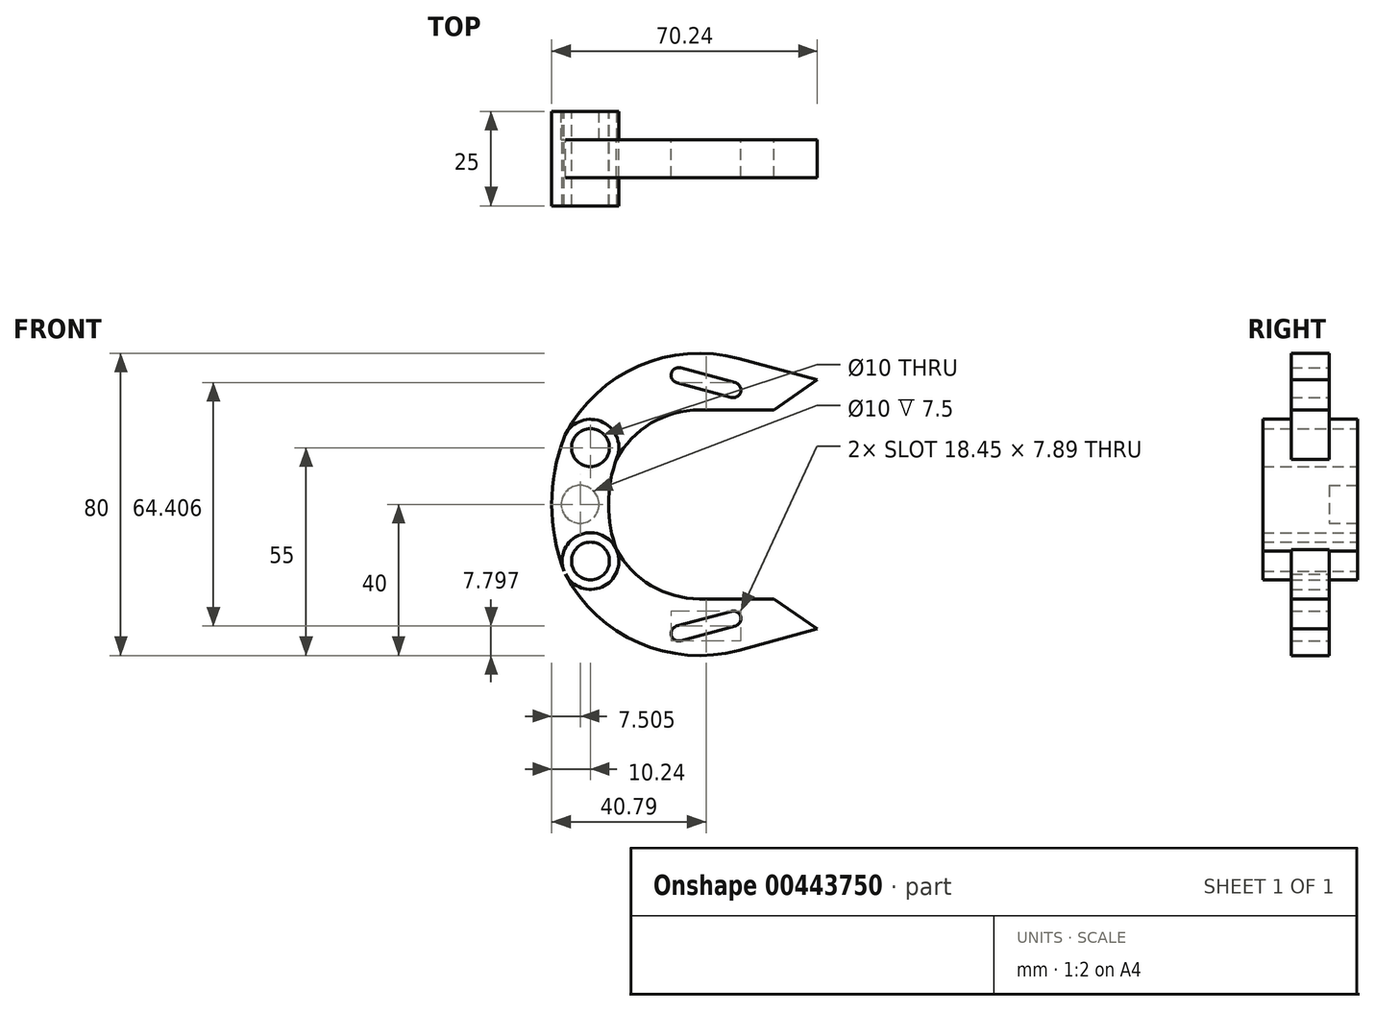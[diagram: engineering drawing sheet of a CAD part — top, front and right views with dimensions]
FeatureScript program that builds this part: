
annotation { "Feature Type Name" : "Feature", "Feature Type Description" : "" }
export const myFeature = defineFeature(function(context is Context, id is Id, definition is map)
    precondition{}
    {
        {
            var Q0;
            Q0=qCreatedBy(makeId("Front.planeOp"),FACE);
            var sketch = newSketch(context, id + "F0", { "sketchPlane" : qUnion([Q0])});
            skLineSegment(sketch, "E0", {"start": v(0, 15) * mm, "end": v(0, -15) * mm, "construction": true});
            skCircle(sketch, "E1", {"center": v(0, 15) * mm, "radius": 7.5 * mm});
            skCircle(sketch, "E2", {"center": v(0, -15) * mm, "radius": 7.5 * mm});
            skArc(sketch, "E3", {"start": v(-7.02, 17.65) * mm, "mid": v(-10.24, 0) * mm, "end": v(-7.02, -17.65) * mm});
            skArc(sketch, "E4", {"start": v(7.02, 12.35) * mm, "mid": v(4.76, 0) * mm, "end": v(7.02, -12.35) * mm});
            skCircle(sketch, "E5", {"center": v(0, 15) * mm, "radius": 5 * mm});
            skCircle(sketch, "E6", {"center": v(0, -15) * mm, "radius": 5 * mm});
            skArc(sketch, "E7", {"start": v(39.29, 38.6) * mm, "mid": v(12.77, 36.63) * mm, "end": v(-6.65, 18.46) * mm});
            skArc(sketch, "E8", {"start": v(28.83, 25) * mm, "mid": v(15.86, 21.37) * mm, "end": v(6.65, 11.54) * mm});
            skLineSegment(sketch, "E9", {"start": v(28.83, 25) * mm, "end": v(48.5, 25) * mm});
            skLineSegment(sketch, "E10", {"start": v(48.5, 25) * mm, "end": v(60, 33) * mm});
            skLineSegment(sketch, "E11", {"start": v(60, 33) * mm, "end": v(39.29, 38.6) * mm});
            skLineSegment(sketch, "E12", {"start": v(39.29, 38.6) * mm, "end": v(37.79, 30.24) * mm, "construction": true});
            skLineSegment(sketch, "E13", {"start": v(37.79, 30.24) * mm, "end": v(23.31, 34.16) * mm, "construction": true});
            skArc(sketch, "E14", {"start": v(23.83, 36.1) * mm, "mid": v(21.38, 34.69) * mm, "end": v(22.79, 32.23) * mm});
            skArc(sketch, "E15", {"start": v(37.27, 28.31) * mm, "mid": v(39.74, 29.8) * mm, "end": v(38.14, 32.21) * mm});
            skLineSegment(sketch, "E16.0", {"start": v(37.27, 28.31) * mm, "end": v(22.79, 32.23) * mm});
            skLineSegment(sketch, "E17.0", {"start": v(38.31, 32.17) * mm, "end": v(23.83, 36.1) * mm});
            skLineSegment(sketch, "E18.MirrorCS", {"start": v(38.31, -32.17) * mm, "end": v(23.83, -36.1) * mm});
            skLineSegment(sketch, "E19.MirrorCS", {"start": v(37.79, -30.24) * mm, "end": v(23.31, -34.16) * mm, "construction": true});
            skArc(sketch, "E20.MirrorCS", {"start": v(23.83, -36.1) * mm, "mid": v(21.38, -34.69) * mm, "end": v(22.79, -32.23) * mm});
            skLineSegment(sketch, "E21.MirrorCS", {"start": v(60, -33) * mm, "end": v(39.29, -38.6) * mm});
            skArc(sketch, "E22.MirrorCS", {"start": v(39.29, -38.6) * mm, "mid": v(12.77, -36.63) * mm, "end": v(-6.65, -18.46) * mm});
            skLineSegment(sketch, "E23.MirrorCS", {"start": v(48.5, -25) * mm, "end": v(60, -33) * mm});
            skArc(sketch, "E24.MirrorCS", {"start": v(37.27, -28.31) * mm, "mid": v(39.74, -29.8) * mm, "end": v(38.14, -32.21) * mm});
            skArc(sketch, "E25.MirrorCS", {"start": v(28.83, -25) * mm, "mid": v(15.86, -21.37) * mm, "end": v(6.65, -11.54) * mm});
            skLineSegment(sketch, "E26.MirrorCS", {"start": v(28.83, -25) * mm, "end": v(48.5, -25) * mm});
            skLineSegment(sketch, "E27.MirrorCS", {"start": v(37.27, -28.31) * mm, "end": v(22.79, -32.23) * mm});
            skLineSegment(sketch, "E28.MirrorCS", {"start": v(39.29, -38.6) * mm, "end": v(37.79, -30.24) * mm, "construction": true});
            skSolve(sketch);
        }
        {
            var Q0;
            {var subQ0=sQuery(id+"F0.wireOp",EDGE,"E4");var subQ1=sQuery(id+"F0.wireOp",EDGE,"E1");var subQ2=makeQuery(id+"F0.imprint","INTERSECT",VERTEX,{"derivedFrom":[subQ1,subQ0]});Q0=makeQuery(id+"F0.imprint","IMPRINT",FACE,{"disambiguationData":[TD([[makeQuery(id+"F0.imprint","IMPRINT",EDGE,{"disambiguationData":[TD([[subQ2,1.0]])],"derivedFrom":subQ1}),-1.0]])]});}
            var Q1;
            {var subQ0=sQuery(id+"F0.wireOp",EDGE,"E2");var subQ1=sQuery(id+"F0.wireOp",EDGE,"E4");var subQ2=makeQuery(id+"F0.imprint","INTERSECT",VERTEX,{"derivedFrom":[subQ1,subQ0]});Q1=makeQuery(id+"F0.imprint","IMPRINT",FACE,{"disambiguationData":[TD([[makeQuery(id+"F0.imprint","IMPRINT",EDGE,{"disambiguationData":[TD([[subQ2,1.0]])],"derivedFrom":subQ1}),-1.0]])]});}
            var Q2;
            Q2=makeQuery(id+"F0.imprint","IMPRINT",FACE,{"disambiguationData":[TD([[makeQuery(id+"F0.imprint","IMPRINT",EDGE,{"derivedFrom":sQuery(id+"F0.wireOp",EDGE,"E6")}),1.0]])]});
            var Q3;
            {var subQ0=sQuery(id+"F0.wireOp",EDGE,"E3");Q3=makeQuery(id+"F0.imprint","IMPRINT",FACE,{"disambiguationData":[TD([[makeQuery(id+"F0.imprint","IMPRINT",EDGE,{"derivedFrom":subQ0}),1.0]])]});}
            var Q4;
            Q4=makeQuery(id+"F0.imprint","IMPRINT",FACE,{"disambiguationData":[TD([[makeQuery(id+"F0.imprint","IMPRINT",EDGE,{"derivedFrom":sQuery(id+"F0.wireOp",EDGE,"E5")}),-1.0]])]});
            extrude(context, id + "F1", {"entities" : qUnion([Q0, Q1, Q2, Q3, Q4]), "endBound" : BoundingType.SYMMETRIC, "depth" : 25 * mm});
        }
        {
            var Q0;
            {var subQ3=sQuery(id+"F0.wireOp",EDGE,"E18.MirrorCS");Q0=makeQuery(id+"F0.imprint","IMPRINT",FACE,{"disambiguationData":[TD([[makeQuery(id+"F0.imprint","IMPRINT",EDGE,{"derivedFrom":subQ3}),1.0]])]});}
            var Q1;
            {var subQ5=sQuery(id+"F0.wireOp",EDGE,"E7");Q1=makeQuery(id+"F0.imprint","IMPRINT",FACE,{"disambiguationData":[TD([[makeQuery(id+"F0.imprint","IMPRINT",EDGE,{"derivedFrom":subQ5}),1.0]])]});}
            extrude(context, id + "F2", {"entities" : qUnion([Q0, Q1]), "operationType" : NewBodyOperationType.ADD, "endBound" : BoundingType.SYMMETRIC, "depth" : 10 * mm});
        }
        {
            var Q0;
            Q0=makeQuery(id+"F1.opExtrude","CAP_FACE",FACE,{"disambiguationData":[OSD([sQuery(id+"F0.wireOp",EDGE,"E1"),sQuery(id+"F0.wireOp",EDGE,"E3"),sQuery(id+"F0.wireOp",EDGE,"E4"),sQuery(id+"F0.wireOp",EDGE,"E5"),sQuery(id+"F0.wireOp",EDGE,"E2"),sQuery(id+"F0.wireOp",EDGE,"E6")])],"isStart":true});
            var sketch = newSketch(context, id + "F3", { "sketchPlane" : qUnion([Q0])});
            skArc(sketch, "E29", {"start": v(0, -15) * mm, "mid": v(2.74, 0) * mm, "end": v(0, 15) * mm, "construction": true});
            skCircle(sketch, "E30", {"center": v(2.74, 0) * mm, "radius": 5 * mm});
            skSolve(sketch);
        }
        {
            var Q0;
            Q0=makeQuery(id+"F3.imprint","IMPRINT",FACE,{"disambiguationData":[TD([[makeQuery(id+"F3.imprint","IMPRINT",EDGE,{"derivedFrom":sQuery(id+"F3.wireOp",EDGE,"E30")}),-1.0]])]});
            var sketch = newSketch(context, id + "F4", { "sketchPlane" : qUnion([Q0])});
            skSolve(sketch);
        }
        {
            var Q0;
            Q0=makeQuery(id+"F3.imprint","IMPRINT",FACE,{"disambiguationData":[TD([[makeQuery(id+"F3.imprint","IMPRINT",EDGE,{"derivedFrom":sQuery(id+"F3.wireOp",EDGE,"E30")}),1.0]])]});
            extrude(context, id + "F5", {"entities" : qUnion([Q0]), "operationType" : NewBodyOperationType.REMOVE, "endBound" : BoundingType.SYMMETRIC, "oppositeDirection" : true, "depth" : 15 * mm});
        }
    });
